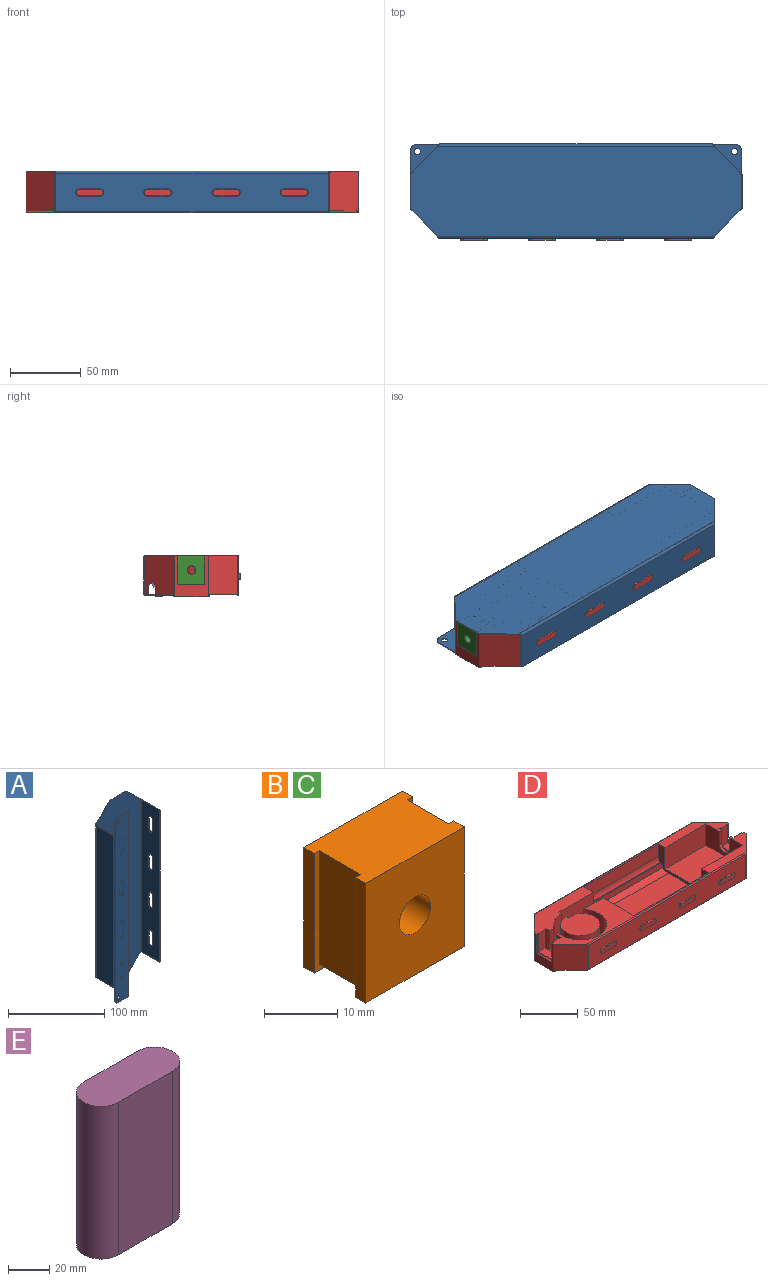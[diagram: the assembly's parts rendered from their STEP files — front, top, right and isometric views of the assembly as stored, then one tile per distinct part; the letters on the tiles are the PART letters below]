
ASSEMBLY  parts=5 mates=4
PART A: 68 faces, bbox 67.6x28.7x235 mm
  f0: plane 193x27.09mm, normal (1,0,0), area 4850.4mm2, adj f6,f14,f22,f23,f44,f45,f52,f53
  f1: plane 194.19x27.09mm, normal (-1,0,0), area 4882.5mm2, adj f6,f13,f22,f23,f44,f45,f52,f53
  f2: plane 235x18.98mm, normal (0,-1,0), area 3989.6mm2, adj f4,f5,f17,f19,f24,f25,f26,f27
  f3: plane 235x20.25mm, normal (0,1,0), area 4033.2mm2, adj f4,f5,f9,f17,f19,f20,f21,f24
  f4: plane 14.48x0.61mm, normal (0,0,1), area 8.8mm2, adj f2,f3,f26,f51
  f5: cylinder r=1.63mm len=231.46mm, axis (0,0,-1), area 545.8mm2, adj f2,f3,f8,f20,f21,f26,f27
  f6: plane 192.48x0.61mm, normal (0,-1,0), area 117.1mm2, adj f0,f1,f44,f45
  f7: plane 235x63.97mm, normal (0,1,0), area 14256.3mm2, adj f14,f15,f16,f18,f20,f21,f22,f23
  f8: plane 193x25.47mm, normal (-1,0,0), area 4915.3mm2, adj f5,f15,f20,f21
  f9: cylinder r=1.02mm len=196.16mm, axis (0,0,-1), area 311.1mm2, adj f3,f10,f20,f21
  f10: plane 194.19x25.47mm, normal (1,0,0), area 4945.5mm2, adj f9,f11,f20,f21
  f11: cylinder r=1.02mm len=196.16mm, axis (0,0,-1), area 311.1mm2, adj f10,f12,f20,f21
  f12: plane 235x63.97mm, normal (0,-1,0), area 14256.3mm2, adj f11,f13,f16,f18,f20,f21,f22,f23
  f13: cylinder r=1.02mm len=196.16mm, axis (0,0,-1), area 311.1mm2, adj f1,f12,f22,f23
  f14: cylinder r=1.63mm len=196.16mm, axis (0,0,-1), area 495.9mm2, adj f0,f7,f22,f23
  f15: cylinder r=1.63mm len=196.16mm, axis (0,0,-1), area 495.9mm2, adj f7,f8,f20,f21
  f16: plane 23.51x0.61mm, normal (0,0,1), area 14.3mm2, adj f7,f12,f46,f47
  f17: plane 14.48x0.61mm, normal (0,0,-1), area 8.8mm2, adj f2,f3,f27,f50
  f18: plane 23.51x0.61mm, normal (0,0,-1), area 14.3mm2, adj f7,f12,f48,f49
  f19: plane 233.78x0.61mm, normal (1,0,0), area 142.6mm2, adj f2,f3,f50,f51
  f20: plane 28.11x21.43mm, normal (-0.7,0,0.72), area 41.3mm2, adj f3,f5,f7,f8,f9,f10,f11,f12
  f21: plane 28.11x21.43mm, normal (-0.7,0,-0.72), area 41.3mm2, adj f3,f5,f7,f8,f9,f10,f11,f12
  f22: plane 28.11x21.43mm, normal (0.7,0,-0.72), area 41.1mm2, adj f0,f1,f7,f12,f13,f14,f45,f49
  f23: plane 28.11x21.43mm, normal (0.7,0,0.72), area 41.1mm2, adj f0,f1,f7,f12,f13,f14,f44,f47
  f24: cylinder r=2.25mm len=4.5mm, axis (0,1,0), area 8.6mm2, adj f2,f3
  f25: cylinder r=2.25mm len=4.5mm, axis (0,1,0), area 8.6mm2, adj f2,f3
  f26: cylinder r=5.16mm len=5.16mm, axis (0,1,0), area 3.8mm2, adj f2,f3,f4,f5
  f27: cylinder r=5.16mm len=5.16mm, axis (0,1,0), area 3.8mm2, adj f2,f3,f5,f17
  f28: cylinder r=2.81mm len=5.61mm, axis (0,1,0), area 5.4mm2, adj f2,f3,f29,f31
  f29: plane 15x0.61mm, normal (-1,0,0), area 9.1mm2, adj f2,f3,f28,f30
  f30: cylinder r=2.81mm len=5.61mm, axis (0,1,0), area 5.4mm2, adj f2,f3,f29,f31
  f31: plane 15x0.61mm, normal (1,0,0), area 9.1mm2, adj f2,f3,f28,f30
  f32: plane 15x0.61mm, normal (-1,0,0), area 9.1mm2, adj f2,f3,f33,f35
  f33: cylinder r=2.81mm len=5.61mm, axis (0,1,0), area 5.4mm2, adj f2,f3,f32,f34
  f34: plane 15x0.61mm, normal (1,0,0), area 9.1mm2, adj f2,f3,f33,f35
  f35: cylinder r=2.81mm len=5.61mm, axis (0,1,0), area 5.4mm2, adj f2,f3,f32,f34
  f36: cylinder r=2.81mm len=5.61mm, axis (0,1,0), area 5.4mm2, adj f2,f3,f37,f39
  f37: plane 15x0.61mm, normal (1,0,0), area 9.1mm2, adj f2,f3,f36,f38
  f38: cylinder r=2.81mm len=5.61mm, axis (0,1,0), area 5.4mm2, adj f2,f3,f37,f39
  f39: plane 15x0.61mm, normal (-1,0,0), area 9.1mm2, adj f2,f3,f36,f38
  f40: cylinder r=2.81mm len=5.61mm, axis (0,1,0), area 5.4mm2, adj f2,f3,f41,f43
  f41: plane 15x0.61mm, normal (1,0,0), area 9.1mm2, adj f2,f3,f40,f42
  f42: cylinder r=2.81mm len=5.61mm, axis (0,1,0), area 5.4mm2, adj f2,f3,f41,f43
  f43: plane 15x0.61mm, normal (-1,0,0), area 9.1mm2, adj f2,f3,f40,f42
  f44: cylinder r=0.61mm len=1.46mm, axis (-0.72,0,0.7), area 0.8mm2, adj f0,f1,f6,f23
  f45: cylinder r=0.61mm len=1.46mm, axis (0.72,0,0.7), area 0.8mm2, adj f0,f1,f6,f22
  f46: cylinder r=0.61mm len=0.61mm, axis (0,1,0), area 0.3mm2, adj f7,f12,f16,f20
  f47: cylinder r=0.61mm len=0.61mm, axis (0,-1,0), area 0.3mm2, adj f7,f12,f16,f23
  f48: cylinder r=0.61mm len=0.61mm, axis (0,1,0), area 0.3mm2, adj f7,f12,f18,f21
  f49: cylinder r=0.61mm len=0.61mm, axis (0,-1,0), area 0.3mm2, adj f7,f12,f18,f22
  f50: cylinder r=0.61mm len=0.61mm, axis (0,1,0), area 0.6mm2, adj f2,f3,f17,f19
  f51: cylinder r=0.61mm len=0.61mm, axis (0,-1,0), area 0.6mm2, adj f2,f3,f4,f19
  f52: cylinder r=2.5mm len=5mm, axis (1,0,0), area 4.8mm2, adj f0,f1,f53,f55
  f53: plane 15x0.61mm, normal (0,1,0), area 9.1mm2, adj f0,f1,f52,f54
  f54: cylinder r=2.5mm len=5mm, axis (1,0,0), area 4.8mm2, adj f0,f1,f53,f55
  f55: plane 15x0.61mm, normal (0,-1,0), area 9.1mm2, adj f0,f1,f52,f54
  f56: cylinder r=2.5mm len=5mm, axis (1,0,0), area 4.8mm2, adj f0,f1,f57,f59
  f57: plane 15x0.61mm, normal (0,-1,0), area 9.1mm2, adj f0,f1,f56,f58
  f58: cylinder r=2.5mm len=5mm, axis (1,0,0), area 4.8mm2, adj f0,f1,f57,f59
  f59: plane 15x0.61mm, normal (0,1,0), area 9.1mm2, adj f0,f1,f56,f58
  f60: cylinder r=2.5mm len=5mm, axis (1,0,0), area 4.8mm2, adj f0,f1,f61,f63
  f61: plane 15x0.61mm, normal (0,-1,0), area 9.1mm2, adj f0,f1,f60,f62
  f62: cylinder r=2.5mm len=5mm, axis (1,0,0), area 4.8mm2, adj f0,f1,f61,f63
  f63: plane 15x0.61mm, normal (0,1,0), area 9.1mm2, adj f0,f1,f60,f62
  f64: cylinder r=2.5mm len=5mm, axis (1,0,0), area 4.8mm2, adj f0,f1,f65,f67
  f65: plane 15x0.61mm, normal (0,-1,0), area 9.1mm2, adj f0,f1,f64,f66
  f66: cylinder r=2.5mm len=5mm, axis (1,0,0), area 4.8mm2, adj f0,f1,f65,f67
  f67: plane 15x0.61mm, normal (0,1,0), area 9.1mm2, adj f0,f1,f64,f66
PART B: 15 faces, bbox 19x12x20 mm
  f0: plane 20x19mm, normal (0,-1,0), area 57mm2, adj f1,f2,f3,f4,f5,f6,f9
  f1: plane 17x8mm, normal (0,0,-1), area 136mm2, adj f0,f4,f5,f7
  f2: plane 19x2mm, normal (0,0,-1), area 38mm2, adj f0,f3,f6,f8
  f3: plane 20x2mm, normal (1,0,0), area 40mm2, adj f0,f2,f8,f9
  f4: plane 19x8mm, normal (1,0,0), area 152mm2, adj f0,f1,f7,f9
  f5: plane 19x8mm, normal (-1,0,0), area 152mm2, adj f0,f1,f7,f9
  f6: plane 20x2mm, normal (-1,0,0), area 40mm2, adj f0,f2,f8,f9
  f7: plane 20x19mm, normal (0,1,0), area 57mm2, adj f1,f4,f5,f9,f10,f11,f12
  f8: plane 20x19mm, normal (0,1,0), area 351.7mm2, adj f2,f3,f6,f9,f13
  f9: plane 19x12mm, normal (0,0,1), area 212mm2, adj f0,f3,f4,f5,f6,f7,f8,f10
  f10: plane 20x2mm, normal (1,0,0), area 40mm2, adj f7,f9,f11,f14
  f11: plane 19x2mm, normal (0,0,-1), area 38mm2, adj f7,f10,f12,f14
  f12: plane 20x2mm, normal (-1,0,0), area 40mm2, adj f7,f9,f11,f14
  f13: cylinder r=3mm len=12mm, axis (0,1,0), area 226.2mm2, adj f8,f14
  f14: plane 20x19mm, normal (0,-1,0), area 351.7mm2, adj f9,f10,f11,f12,f13
PART C: same geometry as B
PART D: 122 faces, bbox 235x67.5x29 mm
  f0: plane 193x25.5mm, normal (0,-1,0), area 4596.9mm2, adj f13,f15,f100,f101,f102,f103,f104,f105
  f1: plane 193x25.5mm, normal (0,1,0), area 4921.5mm2, adj f14,f16,f98,f99
  f2: plane 198x1.5mm, normal (0,0,-1), area 294.8mm2, adj f10,f14,f98,f99
  f3: plane 233.6x12.8mm, normal (0,0,-1), area 2447.7mm2, adj f7,f11,f72,f73,f74,f75,f77,f78
  f4: plane 233.6x19.3mm, normal (0,0,-1), area 4136mm2, adj f8,f13,f100,f101
  f5: plane 235x27.35mm, normal (0,0,1), area 1912.1mm2, adj f16,f17,f18,f19,f23,f25,f28,f29
  f6: plane 235x39mm, normal (0,0,1), area 1987.2mm2, adj f15,f18,f19,f23,f24,f27,f28,f32
  f7: plane 233.6x1.5mm, normal (0,1,0), area 350.4mm2, adj f3,f9,f98,f99
  f8: plane 233.6x1.5mm, normal (0,-1,0), area 350.4mm2, adj f4,f9,f100,f101
  f9: plane 235x25.4mm, normal (0,0,-1), area 5968mm2, adj f7,f8,f23,f46,f98,f99,f100,f101
  f10: plane 198x6mm, normal (0,-1,0), area 1188mm2, adj f2,f12,f98,f99
  f11: plane 208x6mm, normal (0,1,0), area 1134.5mm2, adj f3,f12,f18,f19,f20,f98,f99
  f12: cylinder r=2.5mm len=208mm, axis (1,0,0), area 1161.7mm2, adj f10,f11,f18,f19,f92,f98,f99
  f13: cylinder r=1mm len=195mm, axis (1,0,0), area 304.3mm2, adj f0,f4,f100,f101
  f14: cylinder r=1mm len=195mm, axis (-1,0,0), area 304.3mm2, adj f1,f2,f98,f99
  f15: cylinder r=1mm len=195mm, axis (-1,0,0), area 304.3mm2, adj f0,f6,f100,f101
  f16: cylinder r=1mm len=195mm, axis (1,0,0), area 304.3mm2, adj f1,f5,f98,f99
  f17: cylinder r=23mm len=20.6mm, axis (0,0,1), area 401.2mm2, adj f5,f34,f38,f96
  f18: plane 61x25mm, normal (1,0,0), area 1200.5mm2, adj f5,f6,f11,f12,f20,f24,f25,f26
  f19: plane 61x25mm, normal (-1,0,0), area 444.8mm2, adj f5,f6,f11,f12,f20,f24,f25,f26
  f20: cylinder r=12mm len=91mm, axis (-1,0,0), area 680.1mm2, adj f11,f18,f19,f26
  f21: plane 6.16x0.6mm, normal (1,0,0), area 3.7mm2, adj f37,f38,f69,f94
  f22: plane 17.03x8mm, normal (0,0,1), area 136.2mm2, adj f60,f61,f62,f66
  f23: plane 29x24mm, normal (1,0,0), area 315.5mm2, adj f5,f6,f9,f47,f55,f68,f98,f100
  f24: plane 91x13mm, normal (0,1,0), area 1183mm2, adj f6,f18,f19,f91
  f25: plane 91x13mm, normal (0,-1,0), area 1183mm2, adj f5,f18,f19,f92
  f26: plane 91x37mm, normal (0,0,1), area 3367mm2, adj f18,f19,f20,f91
  f27: plane 50x22.5mm, normal (0,1,0), area 1125mm2, adj f6,f19,f28,f30
  f28: plane 45x22.5mm, normal (-1,0,0), area 801.8mm2, adj f5,f6,f27,f29,f30,f44,f45,f97
  f29: plane 50x22.5mm, normal (0,-1,0), area 1125mm2, adj f5,f19,f28,f30
  f30: plane 50x45mm, normal (0,0,1), area 2250mm2, adj f19,f27,f28,f29
  f31: plane 42x21.4mm, normal (0,-1,0), area 898.8mm2, adj f5,f18,f33,f34
  f32: plane 23.93x21.44mm, normal (0,1,0), area 508.3mm2, adj f6,f18,f33,f35,f96
  f33: plane 42x12mm, normal (0,0,1), area 391.6mm2, adj f18,f31,f32,f34,f96
  f34: plane 21.4x3.11mm, normal (1,0,0), area 64.2mm2, adj f5,f17,f31,f33,f96
  f35: cylinder r=23mm len=46mm, axis (0,0,1), area 1896.9mm2, adj f6,f32,f37,f96
  f36: cylinder r=17mm len=34mm, axis (0,0,1), area 2301.4mm2, adj f39,f40,f41,f42,f43
  f37: cylinder r=23mm len=20.6mm, axis (0,0,1), area 63.9mm2, adj f6,f21,f35,f57,f95
  f38: cylinder r=17mm len=20.6mm, axis (0,0,1), area 102.6mm2, adj f5,f17,f21,f69,f93,f95
  f39: plane 40x40mm, normal (0,0,1), area 348.7mm2, adj f36,f96
  f40: plane 21.4x3mm, normal (1,0,0), area 64.2mm2, adj f36,f41,f42,f43
  f41: plane 9.64x3mm, normal (0,0,1), area 19.7mm2, adj f36,f40,f42
  f42: plane 21.4x9.64mm, normal (0,1,0), area 206.4mm2, adj f36,f40,f41,f43
  f43: plane 34x34mm, normal (0,0,1), area 888.3mm2, adj f36,f40,f42
  f44: plane 12.85x2.5mm, normal (0,-1,0), area 32.1mm2, adj f5,f28,f52,f97
  f45: plane 12.85x2.5mm, normal (0,1,0), area 32.1mm2, adj f6,f28,f52,f97
  f46: plane 29x24mm, normal (-1,0,0), area 315.5mm2, adj f5,f6,f9,f58,f59,f67,f99,f101
  f47: plane 20x2mm, normal (0,-1,0), area 40mm2, adj f5,f23,f48,f68
  f48: plane 20x19.03mm, normal (1,0,0), area 57mm2, adj f5,f6,f47,f49,f54,f55,f56,f68
  f49: plane 19x8mm, normal (0,-1,0), area 152mm2, adj f5,f48,f50,f56
  f50: plane 20x19.03mm, normal (-1,0,0), area 57mm2, adj f5,f6,f49,f51,f53,f54,f56,f70
  f51: plane 20x2mm, normal (0,-1,0), area 40mm2, adj f5,f50,f52,f70
  f52: plane 20x19.03mm, normal (1,0,0), area 169.7mm2, adj f5,f6,f44,f45,f51,f53,f70,f97
  f53: plane 20x2mm, normal (0,1,0), area 40mm2, adj f6,f50,f52,f70
  f54: plane 19x8mm, normal (0,1,0), area 152mm2, adj f6,f48,f50,f56
  f55: plane 20x2mm, normal (0,1,0), area 40mm2, adj f6,f23,f48,f68
  f56: plane 17.03x8mm, normal (0,0,1), area 136.2mm2, adj f48,f49,f50,f54
  f57: plane 20x6.45mm, normal (-1,0,0), area 128.9mm2, adj f6,f37,f63,f69
  f58: plane 20x2mm, normal (0,-1,0), area 40mm2, adj f5,f46,f60,f67
  f59: plane 20x2mm, normal (0,1,0), area 40mm2, adj f6,f46,f60,f67
  f60: plane 20x19.03mm, normal (-1,0,0), area 57mm2, adj f5,f6,f22,f58,f59,f61,f66,f67
  f61: plane 19x8mm, normal (0,1,0), area 152mm2, adj f6,f22,f60,f62
  f62: plane 20x19.03mm, normal (1,0,0), area 57mm2, adj f5,f6,f22,f61,f63,f65,f66,f69
  f63: plane 20x2mm, normal (0,1,0), area 40mm2, adj f6,f57,f62,f69
  f64: plane 20x1.86mm, normal (-1,0,0), area 37.2mm2, adj f5,f65,f69,f93
  f65: plane 20x2mm, normal (0,-1,0), area 40mm2, adj f5,f62,f64,f69
  f66: plane 19x8mm, normal (0,-1,0), area 152mm2, adj f5,f22,f60,f62
  f67: plane 19.03x2mm, normal (0,0,1), area 38mm2, adj f46,f58,f59,f60
  f68: plane 19.03x2mm, normal (0,0,1), area 38mm2, adj f23,f47,f48,f55
  f69: plane 19.03x6.6mm, normal (0,0,1), area 43.4mm2, adj f21,f38,f57,f62,f63,f64,f65,f93
  f70: plane 19.03x2mm, normal (0,0,1), area 38mm2, adj f50,f51,f52,f53
  f71: plane 20x5mm, normal (0,0,-1), area 94.6mm2, adj f72,f73,f74,f75
  f72: plane 15x1.5mm, normal (0,-1,0), area 22.5mm2, adj f3,f71,f73,f74
  f73: cylinder r=2.5mm len=5mm, axis (0,0,1), area 11.8mm2, adj f3,f71,f72,f75
  f74: cylinder r=2.5mm len=5mm, axis (0,0,1), area 11.8mm2, adj f3,f71,f72,f75
  f75: plane 15x1.5mm, normal (0,1,0), area 22.5mm2, adj f3,f71,f73,f74
  f76: plane 20x5mm, normal (0,0,-1), area 94.6mm2, adj f77,f78,f79,f80
  f77: plane 15x1.5mm, normal (0,1,0), area 22.5mm2, adj f3,f76,f78,f79
  f78: cylinder r=2.5mm len=5mm, axis (0,0,1), area 11.8mm2, adj f3,f76,f77,f80
  f79: cylinder r=2.5mm len=5mm, axis (0,0,1), area 11.8mm2, adj f3,f76,f77,f80
  f80: plane 15x1.5mm, normal (0,-1,0), area 22.5mm2, adj f3,f76,f78,f79
  f81: plane 20x5mm, normal (0,0,-1), area 94.6mm2, adj f82,f83,f84,f85
  f82: plane 15x1.5mm, normal (0,-1,0), area 22.5mm2, adj f3,f81,f83,f84
  f83: cylinder r=2.5mm len=5mm, axis (0,0,1), area 11.8mm2, adj f3,f81,f82,f85
  f84: cylinder r=2.5mm len=5mm, axis (0,0,1), area 11.8mm2, adj f3,f81,f82,f85
  f85: plane 15x1.5mm, normal (0,1,0), area 22.5mm2, adj f3,f81,f83,f84
  f86: plane 20x5mm, normal (0,0,-1), area 94.6mm2, adj f87,f88,f89,f90
  f87: plane 15x1.5mm, normal (0,1,0), area 22.5mm2, adj f3,f86,f88,f89
  f88: cylinder r=2.5mm len=5mm, axis (0,0,1), area 11.8mm2, adj f3,f86,f87,f90
  f89: cylinder r=2.5mm len=5mm, axis (0,0,1), area 11.8mm2, adj f3,f86,f87,f90
  f90: plane 15x1.5mm, normal (0,-1,0), area 22.5mm2, adj f3,f86,f88,f89
  f91: cylinder r=12mm len=91mm, axis (1,0,0), area 1715.3mm2, adj f18,f19,f24,f26
  f92: cylinder r=12mm len=91mm, axis (-1,0,0), area 586.1mm2, adj f12,f18,f19,f25
  f93: cylinder r=3mm len=20mm, axis (0,0,1), area 128mm2, adj f5,f38,f64,f69
  f94: cylinder r=3mm len=6.16mm, axis (0,1,0), area 18.6mm2, adj f21,f95
  f95: torus R=20mm, axis (0,0,1), area 64.6mm2, adj f37,f38,f94,f96
  f96: torus R=20mm, axis (0,0,1), area 589.9mm2, adj f17,f32,f33,f34,f35,f39,f95
  f97: cylinder r=6mm len=12mm, axis (1,0,0), area 47.1mm2, adj f28,f44,f45,f52
  f98: plane 29x21mm, normal (0.71,0.71,0), area 761.3mm2, adj f1,f2,f3,f5,f7,f9,f10,f11
  f99: plane 29x21mm, normal (-0.71,0.71,0), area 761.3mm2, adj f1,f2,f3,f5,f7,f9,f10,f11
  f100: plane 29x21mm, normal (0.71,-0.71,0), area 817.6mm2, adj f0,f4,f6,f8,f9,f13,f15,f23
  f101: plane 29x21mm, normal (-0.71,-0.71,0), area 817.6mm2, adj f0,f4,f6,f8,f9,f13,f15,f46
  f102: plane 14.5x1.5mm, normal (0,0,1), area 21.8mm2, adj f0,f103,f105,f106
  f103: cylinder r=2.25mm len=4.5mm, axis (0,1,0), area 10.6mm2, adj f0,f102,f104,f106
  f104: plane 14.5x1.5mm, normal (0,0,-1), area 21.8mm2, adj f0,f103,f105,f106
  f105: cylinder r=2.25mm len=4.5mm, axis (0,1,0), area 10.6mm2, adj f0,f102,f104,f106
  f106: plane 19x4.5mm, normal (0,-1,0), area 81.2mm2, adj f102,f103,f104,f105
  f107: cylinder r=2.25mm len=4.5mm, axis (0,1,0), area 10.6mm2, adj f0,f108,f110,f111
  f108: plane 14.5x1.5mm, normal (0,0,-1), area 21.8mm2, adj f0,f107,f109,f111
  f109: cylinder r=2.25mm len=4.5mm, axis (0,1,0), area 10.6mm2, adj f0,f108,f110,f111
  f110: plane 14.5x1.5mm, normal (0,0,1), area 21.8mm2, adj f0,f107,f109,f111
  f111: plane 19x4.5mm, normal (0,-1,0), area 81.2mm2, adj f107,f108,f109,f110
  f112: plane 14.5x1.5mm, normal (0,0,-1), area 21.8mm2, adj f0,f113,f115,f116
  f113: cylinder r=2.25mm len=4.5mm, axis (0,1,0), area 10.6mm2, adj f0,f112,f114,f116
  f114: plane 14.5x1.5mm, normal (0,0,1), area 21.8mm2, adj f0,f113,f115,f116
  f115: cylinder r=2.25mm len=4.5mm, axis (0,1,0), area 10.6mm2, adj f0,f112,f114,f116
  f116: plane 19x4.5mm, normal (0,-1,0), area 81.2mm2, adj f112,f113,f114,f115
  f117: cylinder r=2.25mm len=4.5mm, axis (0,1,0), area 10.6mm2, adj f0,f118,f120,f121
  f118: plane 14.5x1.5mm, normal (0,0,-1), area 21.8mm2, adj f0,f117,f119,f121
  f119: cylinder r=2.25mm len=4.5mm, axis (0,1,0), area 10.6mm2, adj f0,f118,f120,f121
  f120: plane 14.5x1.5mm, normal (0,0,1), area 21.8mm2, adj f0,f117,f119,f121
  f121: plane 19x4.5mm, normal (0,-1,0), area 81.2mm2, adj f117,f118,f119,f120
PART E: 6 faces, bbox 61x24x91 mm
  f0: plane 91x37mm, normal (0,-1,0), area 3367mm2, adj f2,f3,f4,f5
  f1: plane 91x37mm, normal (0,1,0), area 3367mm2, adj f2,f3,f4,f5
  f2: plane 61x24mm, normal (0,0,1), area 1340.4mm2, adj f0,f1,f4,f5
  f3: plane 61x24mm, normal (0,0,-1), area 1340.4mm2, adj f0,f1,f4,f5
  f4: cylinder r=12mm len=91mm, axis (0,0,-1), area 3430.6mm2, adj f0,f1,f2,f3
  f5: cylinder r=12mm len=91mm, axis (0,0,-1), area 3430.6mm2, adj f0,f1,f2,f3
PLACE A rot(axis=(0.58,-0.58,-0.58),120deg) t=(117.5,0,0.89)mm
PLACE B rot(axis=(0,0,1),90deg) t=(105.5,0,29)mm
PLACE C rot(axis=(0,0,1),90deg) t=(-117.5,0,29)mm
PLACE D t=(0,0,1.5)mm
PLACE E rot(axis=(-0.58,-0.58,0.58),120deg) t=(53,0,16)mm
MATE fastened E.f1 <-> D.f26  axis (0,0,-1) through (7.5,0,4)mm
MATE fastened D.f22 <-> C.f1  axis (0,0,1) through (-111.5,0,10)mm
MATE fastened D.f56 <-> B.f1  axis (0,0,1) through (111.5,0,10)mm
MATE fastened A.f10 <-> D.f1  axis (0,-1,0) through (0,33,15.25)mm
